# Revit family: Franke_Kühleinheit_KE200_EC-A200_MS_EC
name_source: partatom
category: Sonderausstattung
revit_build: Autodesk Revit 2015 (Build: 20140606_1530(x64)
units: mm (PartAtom-declared; Revit-internal decimal feet)

## types (1)
- Kühleinheit KE200 EC-A200 MS EC(230V/EU)
    Anzahl der Nullleiter = 1
    Anzahl der Schutzleiter = 1
    Anzahl von Polen = 1
    Aufstellgewicht = 13 kg
    Bauelement = Beistellgerät Kühleinheit
    Baugruppenkennzeichen = Beistellgerät Kühleinheit
    Beschreibung = Beistellgerät Kühleinheit KE200 MS1 dient zum Aufbewahren von gekühlter Milch
    Breite = 225 mm  [stored 0.738189 ft]
    Energieverlust nach DIN18873 = 0.460 kWh/24 h - 230 V
    Hersteller = Franke
    Höhe = 337 mm  [stored 1.10564 ft]
    Kosten = 0 $
    Leistung = 82 W
    Milchvorrat = 4 l
    Modell = 410862 - Kühleinheit KE200 EC - A200 MS EC
    Netzfrequenz = 50 Hz
    Netzfrequenz alternativ = 60 Hz
    Sicherung = 10 A
    Spannung = 230 V
    Temperaturbereich = + 3°C bis + 8°C
    Tiefe = 453 mm  [stored 1.48622 ft]
    URL = http://www.franke.com

note: [stored X ft] marks values corroborated as IEEE doubles in the binary element streams (Revit-internal decimal feet)

## geometry (parser evidence)
native form markers: Extrusion x1
no freeform markers — native parametric forms only
